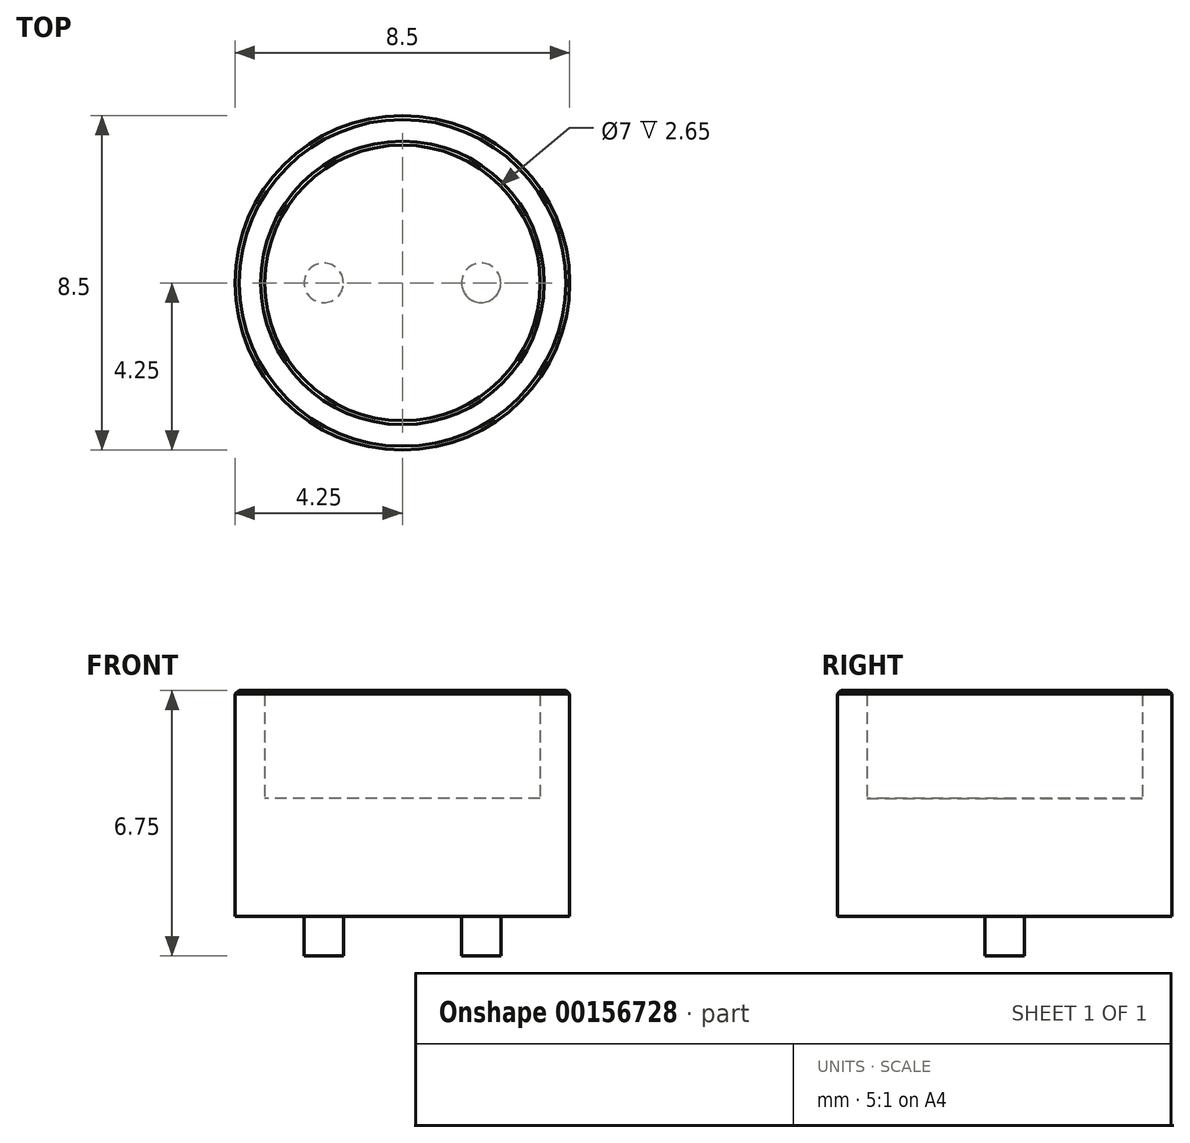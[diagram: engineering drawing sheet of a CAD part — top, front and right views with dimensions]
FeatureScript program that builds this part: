
annotation { "Feature Type Name" : "Feature", "Feature Type Description" : "" }
export const myFeature = defineFeature(function(context is Context, id is Id, definition is map)
    precondition{}
    {
        {
            var Q0;
            Q0=qCreatedBy(makeId("Top.planeOp"),FACE);
            var sketch = newSketch(context, id + "F0", { "sketchPlane" : qUnion([Q0])});
            skCircle(sketch, "E0", {"center": v(0, 0) * mm, "radius": 4.25 * mm});
            skSolve(sketch);
        }
        {
            var Q0;
            Q0=makeQuery(id+"F0.imprint","IMPRINT",FACE,{"disambiguationData":[TD([[makeQuery(id+"F0.imprint","IMPRINT",EDGE,{"derivedFrom":sQuery(id+"F0.wireOp",EDGE,"E0")}),1.0]])]});
            extrude(context, id + "F1", {"entities" : qUnion([Q0]), "depth" : 3 * mm});
        }
        {
            var Q0;
            Q0=makeQuery(id+"F1.opExtrude","CAP_FACE",FACE,{"disambiguationData":[OSD([sQuery(id+"F0.wireOp",EDGE,"E0")])],"isStart":false});
            var sketch = newSketch(context, id + "F2", { "sketchPlane" : qUnion([Q0])});
            skCircle(sketch, "E1", {"center": v(0, 0) * mm, "radius": 3.5 * mm});
            skSolve(sketch);
        }
        {
            var Q0;
            Q0=makeQuery(id+"F2.imprint","IMPRINT",FACE,{"disambiguationData":[TD([[makeQuery(id+"F2.imprint","IMPRINT",EDGE,{"derivedFrom":sQuery(id+"F2.wireOp",EDGE,"E1")}),-1.0]])]});
            extrude(context, id + "F3", {"entities" : qUnion([Q0]), "operationType" : NewBodyOperationType.ADD, "depth" : 2.75 * mm});
        }
        {
            var Q0;
            Q0=makeQuery(id+"F1.opExtrude","CAP_FACE",FACE,{"disambiguationData":[OSD([sQuery(id+"F0.wireOp",EDGE,"E0")])],"isStart":true});
            var sketch = newSketch(context, id + "F4", { "sketchPlane" : qUnion([Q0])});
            skLineSegment(sketch, "E2", {"start": v(0, 0) * mm, "end": v(0, 4.25) * mm, "construction": true});
            skCircle(sketch, "E3", {"center": v(-2, 0) * mm, "radius": 0.5 * mm});
            skCircle(sketch, "E4", {"center": v(2, 0) * mm, "radius": 0.5 * mm});
            skSolve(sketch);
        }
        {
            var Q0;
            Q0 = qSketchRegion(id + "F4", true);
            extrude(context, id + "F5", {"entities" : qUnion([Q0]), "operationType" : NewBodyOperationType.ADD, "depth" : 1 * mm});
        }
        {
            var Q0;
            Q0=makeQuery(id+"F3.opExtrude","CAP_EDGE",EDGE,{"disambiguationData":[OSD([sQuery(id+"F2.wireOp",EDGE,"E1")])],"isStart":false});
            var Q1;
            Q1=makeQuery(id+"F3.opExtrude","CAP_EDGE",EDGE,{"disambiguationData":[OSD([sQuery(id+"F0.wireOp",EDGE,"E0")])],"isStart":false});
            chamfer(context, id + "F6", {"entities" : qUnion([Q0, Q1]), "width" : .1 * mm, "tangentPropagation" : true});
        }
    });
